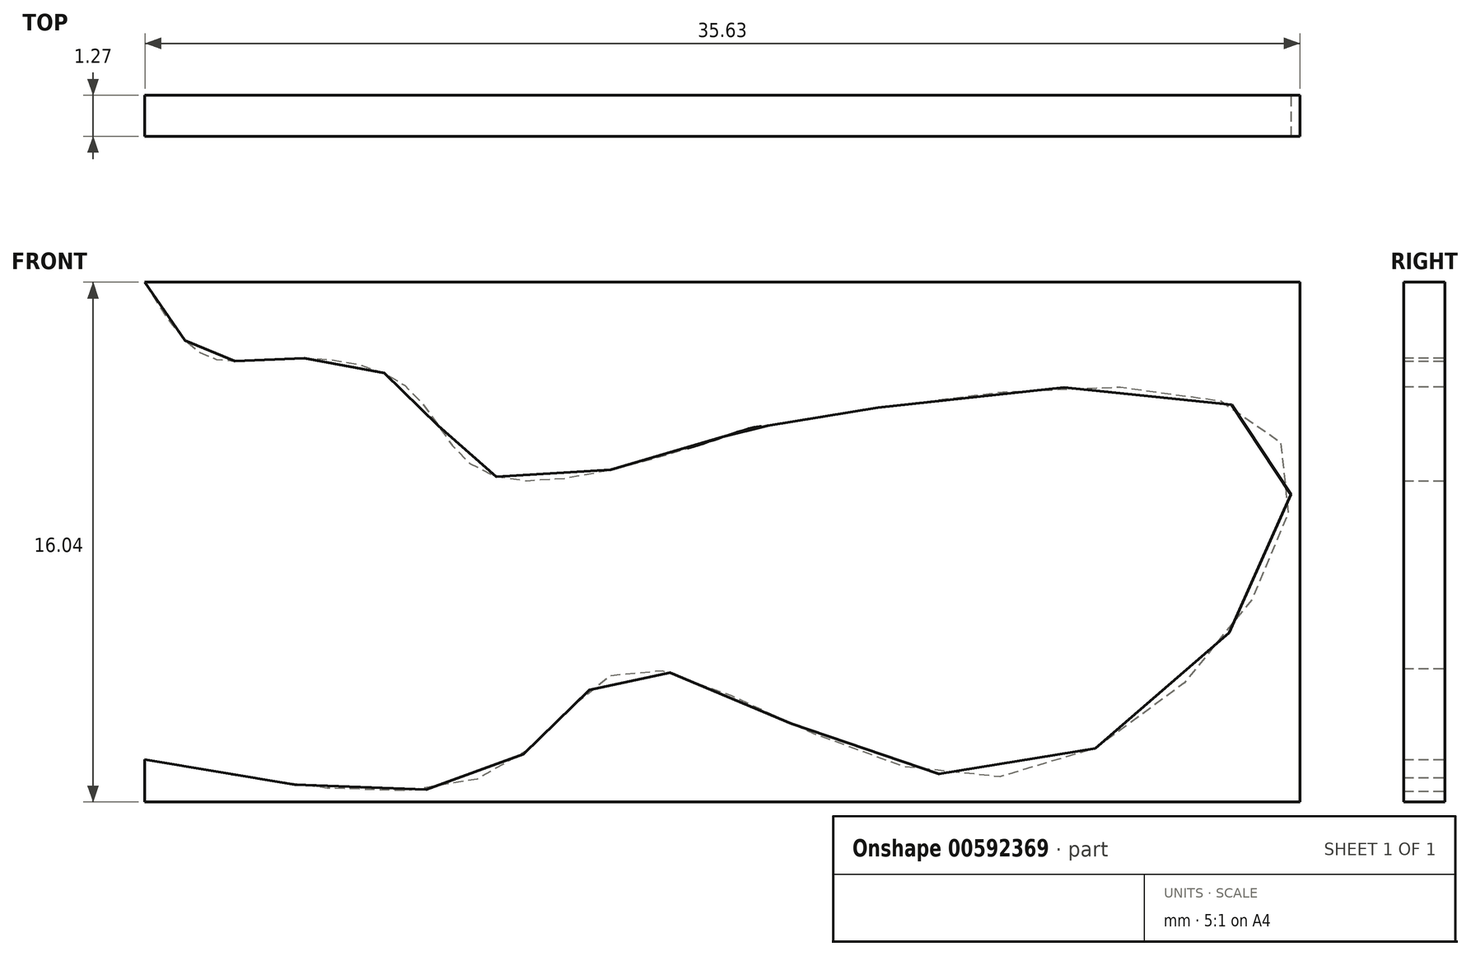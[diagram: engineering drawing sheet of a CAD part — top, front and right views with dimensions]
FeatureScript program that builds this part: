
annotation { "Feature Type Name" : "Feature", "Feature Type Description" : "" }
export const myFeature = defineFeature(function(context is Context, id is Id, definition is map)
    precondition{}
    {
        {
            var Q0;
            Q0=qCreatedBy(makeId("Front.planeOp"),FACE);
            var sketch = newSketch(context, id + "F0", { "sketchPlane" : qUnion([Q0])});
            skLineSegment(sketch, "E0", {"start": v(-12.76, 15.62) * mm, "end": v(22.87, 15.62) * mm});
            skPoint(sketch, "E1", {"position": v(-12.76, 15.62) * mm});
            skPoint(sketch, "E2", {"position": v(22.87, 15.62) * mm});
            skPoint(sketch, "E3", {"position": v(-12.76, -0.42) * mm});
            skLineSegment(sketch, "E4", {"start": v(-12.76, 15.62) * mm, "end": v(-12.76, -0.42) * mm});
            skLineSegment(sketch, "E5", {"start": v(-12.76, -0.42) * mm, "end": v(22.87, -0.42) * mm});
            skLineSegment(sketch, "E6", {"start": v(22.87, -0.42) * mm, "end": v(22.87, 15.62) * mm});
            skFitSpline(sketch, "E7", {"points": [v(-12.76, 15.62) * mm, v(-10.94, 13.37) * mm, v(-8.57, 13.27) * mm, v(-4.64, 12.35) * mm, v(-1.9, 9.6) * mm, v(5.74, 11.06) * mm, v(6.7, 11.22) * mm, v(22.04, 11) * mm, v(14.67, 0.52) * mm, v(2.4, 3.7) * mm, v(-1.63, 0.68) * mm, v(-12.76, 0.9) * mm], "startDerivative": vector(27.37, -46.07) * mm, "endDerivative": vector(-108.19, 20.2) * mm});
            skSolve(sketch);
        }
        {
            var Q0;
            Q0=makeQuery(id+"F0.imprint","IMPRINT",FACE,{"disambiguationData":[TD([[makeQuery(id+"F0.imprint","IMPRINT",EDGE,{"derivedFrom":sQuery(id+"F0.wireOp",EDGE,"E0")}),-1.0]])]});
            extrude(context, id + "F1", {"entities" : qUnion([Q0]), "depth" : 1.27 * mm, "offsetDistance" : 25.4 * mm});
        }
    });
